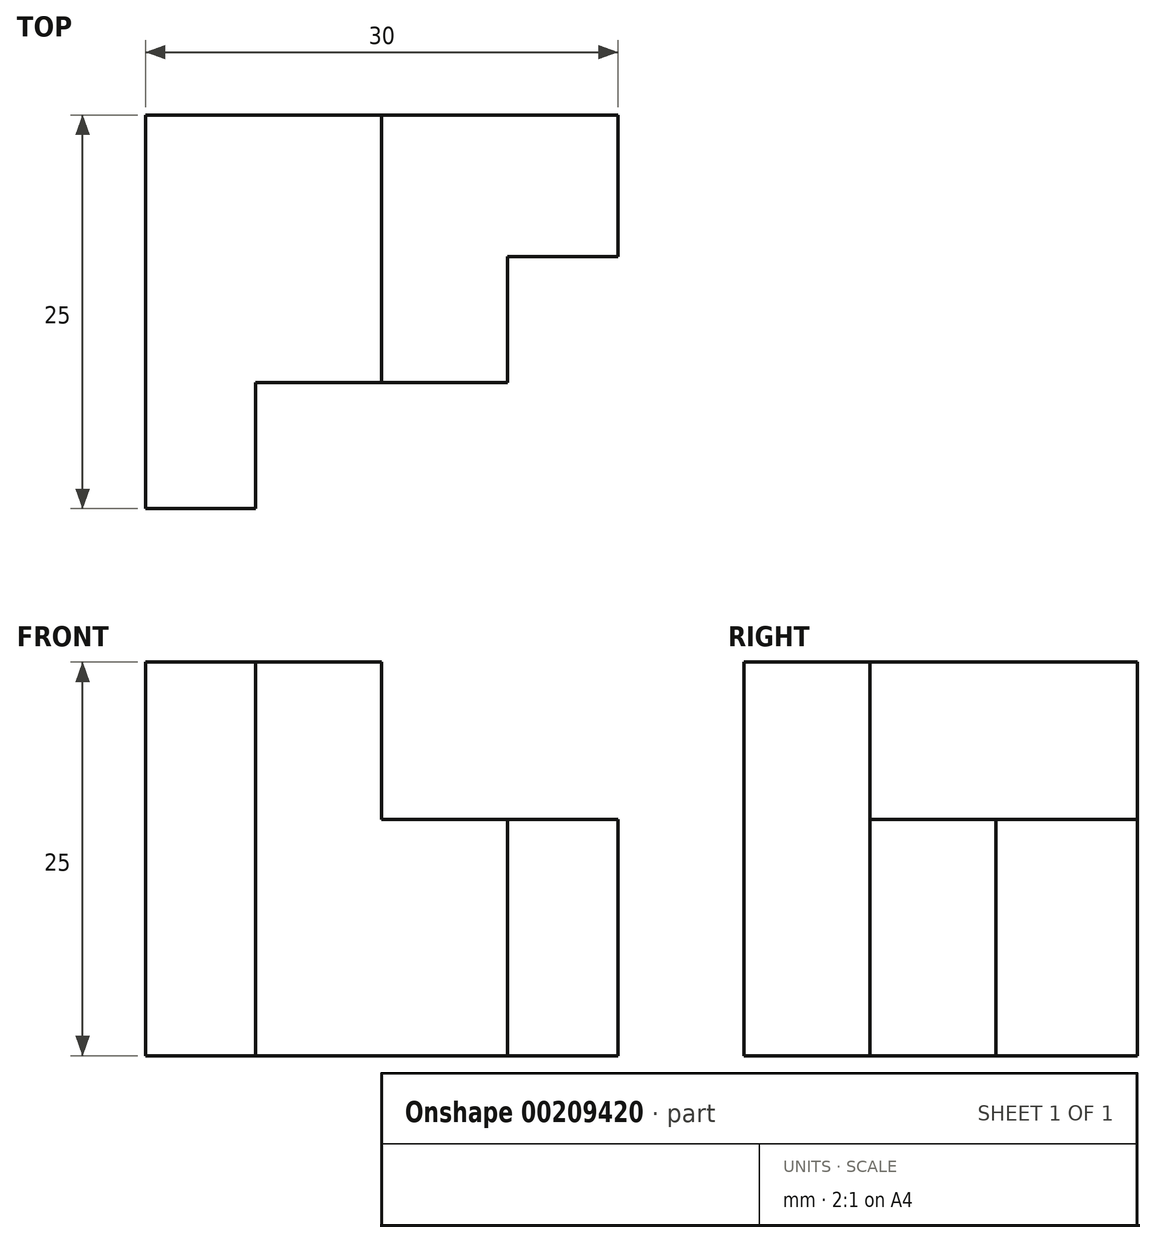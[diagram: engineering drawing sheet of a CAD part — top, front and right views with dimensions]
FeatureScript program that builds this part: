
annotation { "Feature Type Name" : "Feature", "Feature Type Description" : "" }
export const myFeature = defineFeature(function(context is Context, id is Id, definition is map)
    precondition{}
    {
        {
            var Q0;
            Q0=qCreatedBy(makeId("Top.planeOp"),FACE);
            var sketch = newSketch(context, id + "F0", { "sketchPlane" : qUnion([Q0])});
            skLineSegment(sketch, "E0.bottom", {"start": v(0, 0) * mm, "end": v(7, 0) * mm});
            skLineSegment(sketch, "E0.top", {"start": v(0, 25) * mm, "end": v(30, 25) * mm});
            skLineSegment(sketch, "E0.left", {"start": v(0, 0) * mm, "end": v(0, 25) * mm});
            skLineSegment(sketch, "E0.right", {"start": v(30, 16) * mm, "end": v(30, 25) * mm});
            skLineSegment(sketch, "E1", {"start": v(7, 0) * mm, "end": v(7, 8) * mm});
            skLineSegment(sketch, "E2", {"start": v(7, 8) * mm, "end": v(23, 8) * mm});
            skLineSegment(sketch, "E3", {"start": v(23, 8) * mm, "end": v(23, 16) * mm});
            skLineSegment(sketch, "E4", {"start": v(23, 16) * mm, "end": v(30, 16) * mm});
            skSolve(sketch);
        }
        {
            var Q0;
            Q0=makeQuery(id+"F0.imprint","IMPRINT",FACE,{"disambiguationData":[TD([[makeQuery(id+"F0.imprint","IMPRINT",EDGE,{"derivedFrom":sQuery(id+"F0.wireOp",EDGE,"E0.bottom")}),1.0]])]});
            extrude(context, id + "F1", {"entities" : qUnion([Q0]), "depth" : 25 * mm});
        }
        {
            var Q0;
            Q0=makeQuery(id+"F1.opExtrude","SWEPT_FACE",FACE,{"disambiguationData":[OSD([sQuery(id+"F0.wireOp",EDGE,"E0.top")])]});
            var sketch = newSketch(context, id + "F2", { "sketchPlane" : qUnion([Q0])});
            skLineSegment(sketch, "E5.bottom", {"start": v(-30, 25) * mm, "end": v(-15, 25) * mm});
            skLineSegment(sketch, "E5.top", {"start": v(-30, 15) * mm, "end": v(-15, 15) * mm});
            skLineSegment(sketch, "E5.left", {"start": v(-30, 25) * mm, "end": v(-30, 15) * mm});
            skLineSegment(sketch, "E5.right", {"start": v(-15, 25) * mm, "end": v(-15, 15) * mm});
            skSolve(sketch);
        }
        {
            var Q0;
            Q0=makeQuery(id+"F2.imprint","IMPRINT",FACE,{"disambiguationData":[TD([[makeQuery(id+"F2.imprint","IMPRINT",EDGE,{"derivedFrom":sQuery(id+"F2.wireOp",EDGE,"E5.bottom")}),1.0]])]});
            extrude(context, id + "F3", {"entities" : qUnion([Q0]), "operationType" : NewBodyOperationType.REMOVE, "oppositeDirection" : true, "depth" : 25 * mm});
        }
    });
